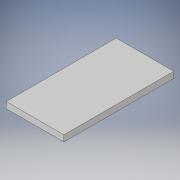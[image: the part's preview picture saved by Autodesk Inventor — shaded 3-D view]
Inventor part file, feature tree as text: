
AUTODESK INVENTOR PART (.ipt)
format: ipt  version: 2019 (Build 230136000, 136)  size: 90,112 bytes
history: native  units: mm
features: extrude x1, sketch x1
ambient origin geometry x8: Origin, YZ Plane, XZ Plane, XY Plane, X Axis, Y Axis, Z Axis, Center Point
bodies: Solid1 (feature_tree)
feature tree (2):
  extrude  "Extrusion1"  Depth=29.54mm
  sketch  "Sketch1"  dims[d0=56.36mm d1=29.54mm d2=3.18mm d3=0.0mm]
